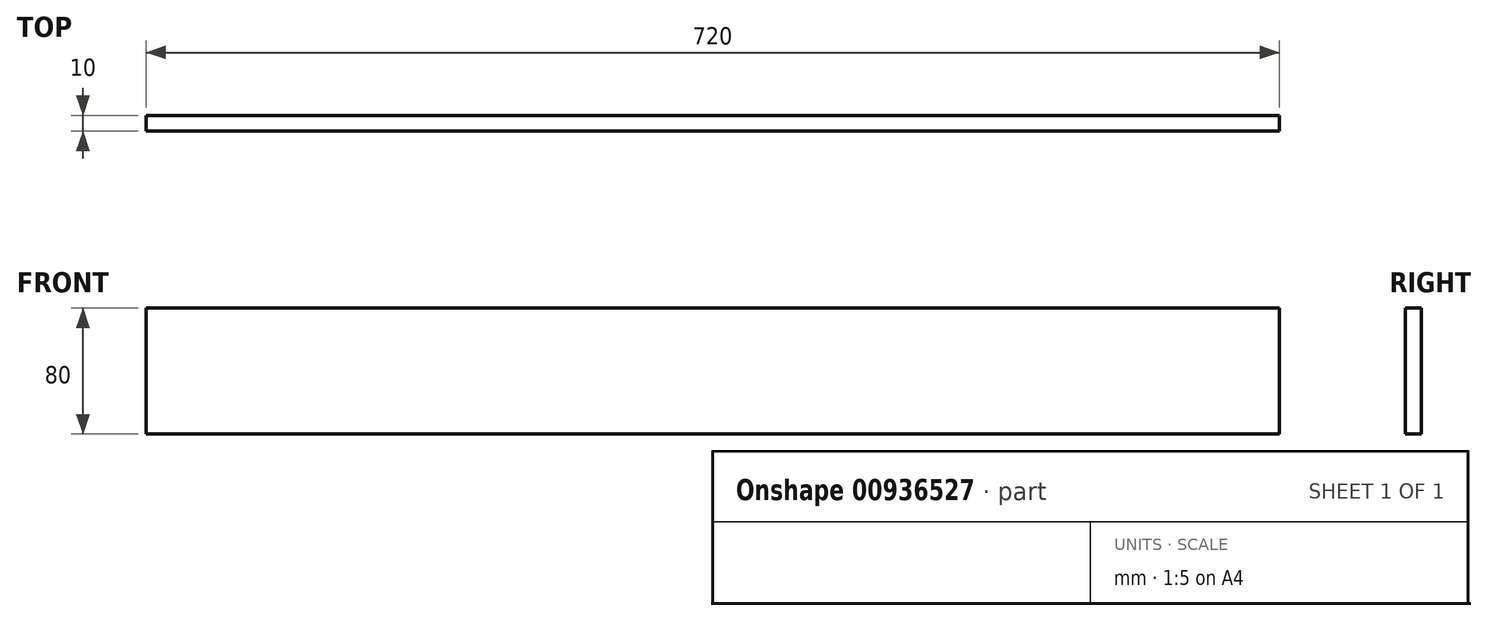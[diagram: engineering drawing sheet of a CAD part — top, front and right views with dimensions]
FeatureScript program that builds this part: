
annotation { "Feature Type Name" : "Feature", "Feature Type Description" : "" }
export const myFeature = defineFeature(function(context is Context, id is Id, definition is map)
    precondition{}
    {
        {
            var Q0;
            Q0=qCreatedBy(makeId("Right.planeOp"),FACE);
            var sketch = newSketch(context, id + "F0", { "sketchPlane" : qUnion([Q0])});
            skLineSegment(sketch, "E0.bottom", {"start": v(0, 0) * mm, "end": v(10, 0) * mm});
            skLineSegment(sketch, "E0.top", {"start": v(0, 80) * mm, "end": v(10, 80) * mm});
            skLineSegment(sketch, "E0.left", {"start": v(0, 0) * mm, "end": v(0, 80) * mm});
            skLineSegment(sketch, "E0.right", {"start": v(10, 0) * mm, "end": v(10, 80) * mm});
            skSolve(sketch);
        }
        {
            var Q0;
            Q0=makeQuery(id+"F0.imprint","IMPRINT",FACE,{"disambiguationData":[TD([[makeQuery(id+"F0.imprint","IMPRINT",EDGE,{"derivedFrom":sQuery(id+"F0.wireOp",EDGE,"E0.bottom")}),1.0]])]});
            extrude(context, id + "F1", {"entities" : qUnion([Q0]), "depth" : 720 * mm, "offsetDistance" : 25 * mm});
        }
    });
